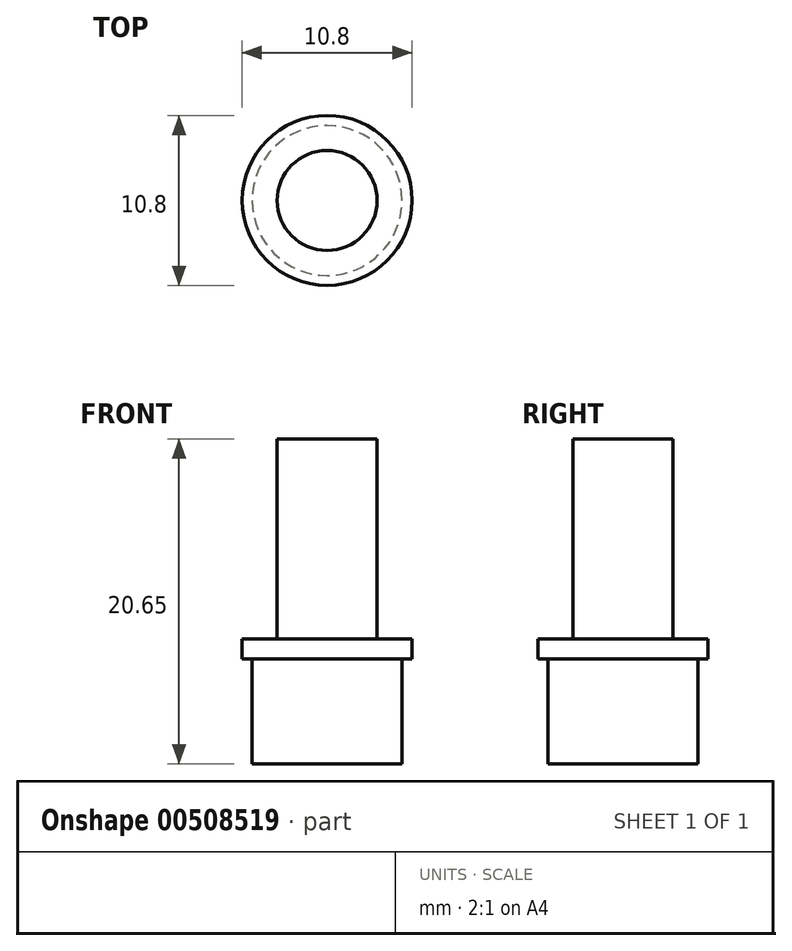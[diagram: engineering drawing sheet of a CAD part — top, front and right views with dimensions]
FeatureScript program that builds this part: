
annotation { "Feature Type Name" : "Feature", "Feature Type Description" : "" }
export const myFeature = defineFeature(function(context is Context, id is Id, definition is map)
    precondition{}
    {
        {
            var Q0;
            Q0=qCreatedBy(makeId("Top.planeOp"),FACE);
            var sketch = newSketch(context, id + "F0", { "sketchPlane" : qUnion([Q0])});
            skCircle(sketch, "E0", {"center": v(0, 0) * mm, "radius": 4.76 * mm});
            skSolve(sketch);
        }
        {
            var Q0;
            Q0=makeQuery(id+"F0.imprint","IMPRINT",FACE,{"disambiguationData":[TD([[makeQuery(id+"F0.imprint","IMPRINT",EDGE,{"derivedFrom":sQuery(id+"F0.wireOp",EDGE,"E0")}),1.0]])]});
            extrude(context, id + "F1", {"entities" : qUnion([Q0]), "depth" : 7.95 * mm, "offsetDistance" : 25.4 * mm});
        }
        {
            var Q0;
            Q0=makeQuery(id+"F1.opExtrude","CAP_FACE",FACE,{"disambiguationData":[OSD([sQuery(id+"F0.wireOp",EDGE,"E0")])],"isStart":false});
            var sketch = newSketch(context, id + "F2", { "sketchPlane" : qUnion([Q0])});
            skCircle(sketch, "E1", {"center": v(0, 0) * mm, "radius": 5.4 * mm});
            skSolve(sketch);
        }
        {
            var Q0;
            Q0=makeQuery(id+"F2.imprint","IMPRINT",FACE,{"disambiguationData":[TD([[makeQuery(id+"F2.imprint","IMPRINT",EDGE,{"derivedFrom":sQuery(id+"F2.wireOp",EDGE,"E1")}),1.0]])]});
            extrude(context, id + "F3", {"entities" : qUnion([Q0]), "operationType" : NewBodyOperationType.ADD, "oppositeDirection" : true, "depth" : 1.27 * mm, "offsetDistance" : 25.4 * mm});
        }
        {
            var Q0;
            Q0=makeQuery(id+"F1.opExtrude","CAP_FACE",FACE,{"disambiguationData":[OSD([sQuery(id+"F0.wireOp",EDGE,"E0")])],"isStart":false});
            var sketch = newSketch(context, id + "F4", { "sketchPlane" : qUnion([Q0])});
            skCircle(sketch, "E2", {"center": v(0, 0) * mm, "radius": 3.17 * mm});
            skSolve(sketch);
        }
        {
            var Q0;
            Q0=makeQuery(id+"F4.imprint","IMPRINT",FACE,{"disambiguationData":[TD([[makeQuery(id+"F4.imprint","IMPRINT",EDGE,{"derivedFrom":sQuery(id+"F4.wireOp",EDGE,"E2")}),1.0]])]});
            extrude(context, id + "F5", {"entities" : qUnion([Q0]), "operationType" : NewBodyOperationType.ADD, "depth" : 12.7 * mm, "offsetDistance" : 25.4 * mm});
        }
    });
